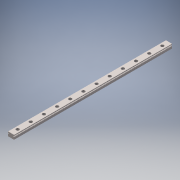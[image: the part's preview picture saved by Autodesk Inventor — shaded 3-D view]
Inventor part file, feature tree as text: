
AUTODESK INVENTOR PART (.ipt)
format: ipt  version: 2018 (Build 220112000, 112)  size: 178,688 bytes
history: native  units: in
note: dims shown in document units (in); Inventor stores cm internally (conversion verified against a paired STEP export)
features: other x1, extrude x1, plane x1, sketch x1
ambient origin geometry x8: Origin, YZ Plane, XZ Plane, XY Plane, X Axis, Y Axis, Z Axis, Center Point
bodies: Solid1 (feature_tree)
feature tree (4):
  other  "Pattern1"
  extrude  "Extrusion1"  Depth=0.7874in
  plane  "Work Plane1"
  sketch  "Sketch1"  dims[d0=3.937in d1=0.7874in d2=0.3937in d3=0.0in]
